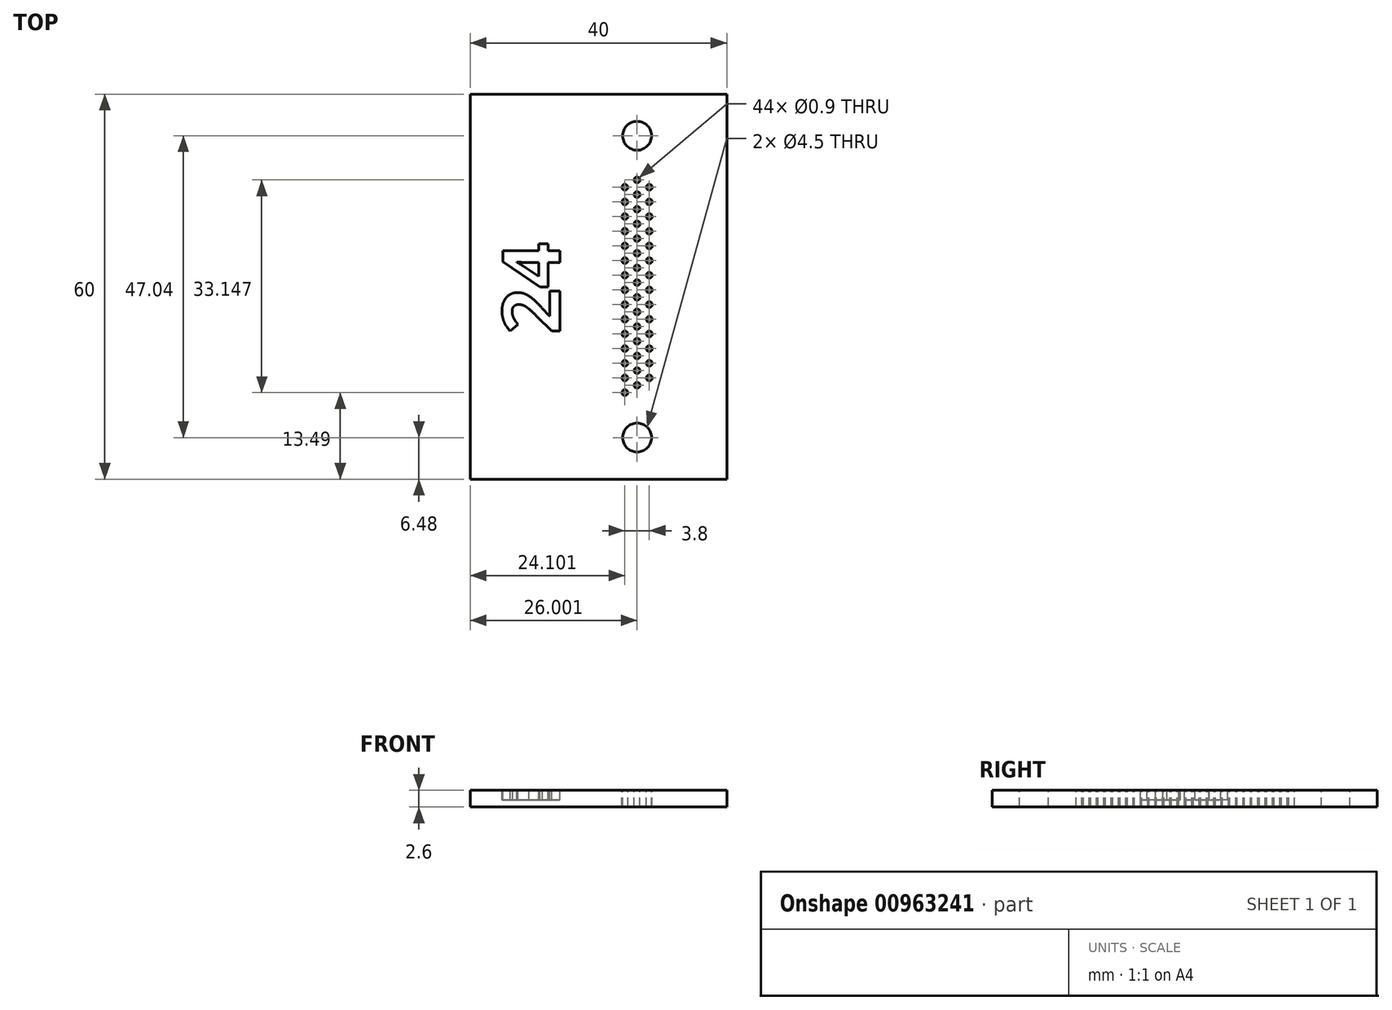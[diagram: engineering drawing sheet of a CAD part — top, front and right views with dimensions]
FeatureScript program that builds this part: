
annotation { "Feature Type Name" : "Feature", "Feature Type Description" : "" }
export const myFeature = defineFeature(function(context is Context, id is Id, definition is map)
    precondition{}
    {
        {
            var Q0;
            Q0=qCreatedBy(makeId("Top.planeOp"),FACE);
            var sketch = newSketch(context, id + "F0", { "sketchPlane" : qUnion([Q0])});
            skLineSegment(sketch, "E0.bottom", {"start": v(-43.16, 38.34) * mm, "end": v(-3.16, 38.34) * mm});
            skLineSegment(sketch, "E0.top", {"start": v(-43.16, -21.66) * mm, "end": v(-3.16, -21.66) * mm});
            skLineSegment(sketch, "E0.left", {"start": v(-43.16, 38.34) * mm, "end": v(-43.16, -21.66) * mm});
            skLineSegment(sketch, "E0.right", {"start": v(-3.16, 38.34) * mm, "end": v(-3.16, -21.66) * mm});
            skSolve(sketch);
        }
        {
            var Q0;
            Q0=makeQuery(id+"F0.imprint","IMPRINT",FACE,{"disambiguationData":[TD([[makeQuery(id+"F0.imprint","IMPRINT",EDGE,{"derivedFrom":sQuery(id+"F0.wireOp",EDGE,"E0.bottom")}),-1.0]])]});
            extrude(context, id + "F1", {"entities" : qUnion([Q0]), "depth" : 2.6 * mm, "offsetDistance" : 25 * mm});
        }
        {
            var Q0;
            Q0=makeQuery(id+"F1.opExtrude","CAP_FACE",FACE,{"disambiguationData":[OSD([sQuery(id+"F0.wireOp",EDGE,"E0.bottom"),sQuery(id+"F0.wireOp",EDGE,"E0.top"),sQuery(id+"F0.wireOp",EDGE,"E0.left"),sQuery(id+"F0.wireOp",EDGE,"E0.right")])],"isStart":false});
            var sketch = newSketch(context, id + "F2", { "sketchPlane" : qUnion([Q0])});
            skText(sketch, "E1", { "text": "24", "fontName": "OpenSans-Bold.ttf"});
            const initialGuessF2  = {"E1": [-0.02916, 0.00094, 0, 1, 0.009]};
            skSetInitialGuess(sketch, initialGuessF2);
            skSolve(sketch);
        }
        {
            var Q0;
            Q0=qSketchRegion(id+"F2",true);
            extrude(context, id + "F3", {"entities" : qUnion([Q0]), "operationType" : NewBodyOperationType.REMOVE, "oppositeDirection" : true, "depth" : 1.5 * mm, "offsetDistance" : 25 * mm});
        }
        {
            var Q0;
            {var subQ0=sQuery(id+"F0.wireOp",EDGE,"E0.left");var subQ1=sQuery(id+"F0.wireOp",EDGE,"E0.bottom");var subQ2=sQuery(id+"F0.wireOp",EDGE,"E0.right");var subQ3=sQuery(id+"F0.wireOp",EDGE,"E0.top");Q0=makeQuery(id+"F3.boolean.opBoolean","SPLIT",FACE,{"disambiguationData":[TD([makeQuery(id+"F1.opExtrude","SWEPT_FACE",FACE,{"disambiguationData":[OSD([subQ1])]})])],"derivedFrom":makeQuery(id+"F1.opExtrude","CAP_FACE",FACE,{"disambiguationData":[OSD([subQ1,subQ3,subQ0,subQ2])],"isStart":false})});}
            var sketch = newSketch(context, id + "F4", { "sketchPlane" : qUnion([Q0])});
            skCircle(sketch, "E2", {"center": v(-19.06, 14.7) * mm, "radius": 0.45 * mm});
            skCircle(sketch, "E3", {"center": v(-19.06, 16.98) * mm, "radius": 0.45 * mm});
            skCircle(sketch, "E4", {"center": v(-19.06, 19.26) * mm, "radius": 0.45 * mm});
            skCircle(sketch, "E5", {"center": v(-19.06, 21.55) * mm, "radius": 0.45 * mm});
            skCircle(sketch, "E6", {"center": v(-19.06, 23.83) * mm, "radius": 0.45 * mm});
            skCircle(sketch, "E7", {"center": v(-17.16, 15.83) * mm, "radius": 0.45 * mm});
            skCircle(sketch, "E8", {"center": v(-17.16, 18.12) * mm, "radius": 0.45 * mm});
            skCircle(sketch, "E9", {"center": v(-17.16, 20.4) * mm, "radius": 0.45 * mm});
            skCircle(sketch, "E10", {"center": v(-17.16, 22.7) * mm, "radius": 0.45 * mm});
            skCircle(sketch, "E11", {"center": v(-17.16, 24.98) * mm, "radius": 0.45 * mm});
            skCircle(sketch, "E12", {"center": v(-15.26, 14.7) * mm, "radius": 0.45 * mm});
            skCircle(sketch, "E13", {"center": v(-15.26, 16.98) * mm, "radius": 0.45 * mm});
            skCircle(sketch, "E14", {"center": v(-15.26, 19.26) * mm, "radius": 0.45 * mm});
            skCircle(sketch, "E15", {"center": v(-15.26, 21.55) * mm, "radius": 0.45 * mm});
            skCircle(sketch, "E16", {"center": v(-15.26, 23.83) * mm, "radius": 0.45 * mm});
            skCircle(sketch, "E17", {"center": v(-19.06, 3.26) * mm, "radius": 0.45 * mm});
            skCircle(sketch, "E18", {"center": v(-19.06, 5.55) * mm, "radius": 0.45 * mm});
            skCircle(sketch, "E19", {"center": v(-19.06, 7.83) * mm, "radius": 0.45 * mm});
            skCircle(sketch, "E20", {"center": v(-19.06, 10.12) * mm, "radius": 0.45 * mm});
            skCircle(sketch, "E21", {"center": v(-19.06, 12.4) * mm, "radius": 0.45 * mm});
            skCircle(sketch, "E22", {"center": v(-17.16, 4.4) * mm, "radius": 0.45 * mm});
            skCircle(sketch, "E23", {"center": v(-17.16, 6.69) * mm, "radius": 0.45 * mm});
            skCircle(sketch, "E24", {"center": v(-17.16, 8.98) * mm, "radius": 0.45 * mm});
            skCircle(sketch, "E25", {"center": v(-17.16, 11.26) * mm, "radius": 0.45 * mm});
            skCircle(sketch, "E26", {"center": v(-17.16, 13.55) * mm, "radius": 0.45 * mm});
            skCircle(sketch, "E27", {"center": v(-15.26, 3.26) * mm, "radius": 0.45 * mm});
            skCircle(sketch, "E28", {"center": v(-15.26, 5.55) * mm, "radius": 0.45 * mm});
            skCircle(sketch, "E29", {"center": v(-15.26, 7.83) * mm, "radius": 0.45 * mm});
            skCircle(sketch, "E30", {"center": v(-15.26, 10.12) * mm, "radius": 0.45 * mm});
            skCircle(sketch, "E31", {"center": v(-15.26, 12.4) * mm, "radius": 0.45 * mm});
            skCircle(sketch, "E32", {"center": v(-19.06, -8.17) * mm, "radius": 0.45 * mm});
            skCircle(sketch, "E33", {"center": v(-19.06, -5.88) * mm, "radius": 0.45 * mm});
            skCircle(sketch, "E34", {"center": v(-19.06, -3.6) * mm, "radius": 0.45 * mm});
            skCircle(sketch, "E35", {"center": v(-19.06, -1.31) * mm, "radius": 0.45 * mm});
            skCircle(sketch, "E36", {"center": v(-19.06, 0.97) * mm, "radius": 0.45 * mm});
            skCircle(sketch, "E37", {"center": v(-17.16, -7.03) * mm, "radius": 0.45 * mm});
            skCircle(sketch, "E38", {"center": v(-17.16, -4.74) * mm, "radius": 0.45 * mm});
            skCircle(sketch, "E39", {"center": v(-17.16, -2.45) * mm, "radius": 0.45 * mm});
            skCircle(sketch, "E40", {"center": v(-17.16, -0.17) * mm, "radius": 0.45 * mm});
            skCircle(sketch, "E41", {"center": v(-17.16, 2.12) * mm, "radius": 0.45 * mm});
            skCircle(sketch, "E42", {"center": v(-15.26, -5.88) * mm, "radius": 0.45 * mm});
            skCircle(sketch, "E43", {"center": v(-15.26, -3.6) * mm, "radius": 0.45 * mm});
            skCircle(sketch, "E44", {"center": v(-15.26, -1.31) * mm, "radius": 0.45 * mm});
            skCircle(sketch, "E45", {"center": v(-15.26, 0.97) * mm, "radius": 0.45 * mm});
            skCircle(sketch, "E46", {"center": v(-17.16, 31.86) * mm, "radius": 2.25 * mm});
            skCircle(sketch, "E47", {"center": v(-17.16, -15.18) * mm, "radius": 2.25 * mm});
            skSolve(sketch);
        }
        {
            var Q0;
            Q0 = qSketchRegion(id + "F4", true);
            extrude(context, id + "F5", {"entities" : qUnion([Q0]), "operationType" : NewBodyOperationType.REMOVE, "endBound" : BoundingType.UP_TO_NEXT, "oppositeDirection" : true, "depth" : 25 * mm, "offsetDistance" : 25 * mm});
        }
    });
